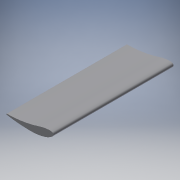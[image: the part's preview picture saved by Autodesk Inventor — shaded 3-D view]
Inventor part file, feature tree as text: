
AUTODESK INVENTOR PART (.ipt)
format: ipt  version: 2018.2 (Build 222227000, 227)  size: 176,128 bytes
history: native  units: mm
features: other x4, extrude x2, sketch x2, fillet x1, mirror x1, projected_geometry x1
ambient origin geometry x8: Origin, YZ Plane, XZ Plane, XY Plane, X Axis, Y Axis, Z Axis, Center Point
bodies: Body1 (feature_tree)
feature tree (11):
  other  "naca97.ipt"
  extrude  "押し出し1"  Depth=110.0mm
  fillet  "フィレット1"  Radius=220.0mm
  extrude  "押し出し2"  Depth=1200.0mm
  mirror  "ミラー1"
  other  "ソリッド1::naca97.ipt"
  other  "TaggingFeature1"
  sketch  "スケッチ1"
  sketch  "スケッチ2"
  projected_geometry  "投影ループ1"
  other  "ソリッド1"
